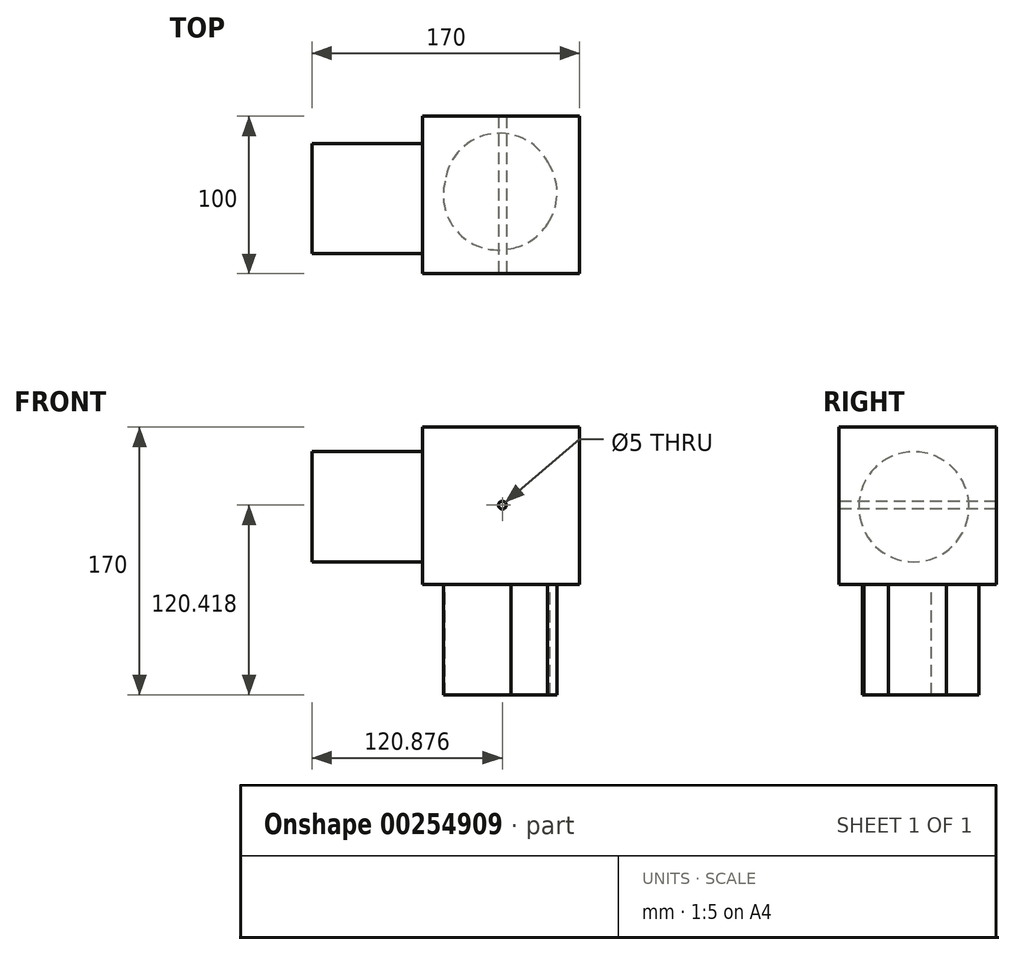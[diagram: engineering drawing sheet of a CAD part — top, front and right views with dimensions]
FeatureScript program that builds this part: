
annotation { "Feature Type Name" : "Feature", "Feature Type Description" : "" }
export const myFeature = defineFeature(function(context is Context, id is Id, definition is map)
    precondition{}
    {
        {
            var Q0;
            Q0=qCreatedBy(makeId("Front.planeOp"),FACE);
            var sketch = newSketch(context, id + "F0", { "sketchPlane" : qUnion([Q0])});
            skLineSegment(sketch, "E0.bottom", {"start": v(0, 0) * mm, "end": v(100, 0) * mm});
            skLineSegment(sketch, "E0.top", {"start": v(0, 100) * mm, "end": v(100, 100) * mm});
            skLineSegment(sketch, "E0.left", {"start": v(0, 0) * mm, "end": v(0, 100) * mm});
            skLineSegment(sketch, "E0.right", {"start": v(100, 0) * mm, "end": v(100, 100) * mm});
            skSolve(sketch);
        }
        {
            var Q0;
            Q0 = qSketchRegion(id + "F0", true);
            extrude(context, id + "F1", {"entities" : qUnion([Q0]), "depth" : 100 * mm});
        }
        {
            var Q0;
            Q0=qCreatedBy(makeId("Top.planeOp"),FACE);
            var sketch = newSketch(context, id + "F2", { "sketchPlane" : qUnion([Q0])});
            skCircle(sketch, "E1", {"center": v(48.35, -50) * mm, "radius": 35 * mm});
            skSolve(sketch);
        }
        {
            var Q0;
            Q0 = qSketchRegion(id + "F2", true);
            extrude(context, id + "F3", {"entities" : qUnion([Q0]), "operationType" : NewBodyOperationType.ADD, "oppositeDirection" : true, "depth" : 70 * mm});
        }
        {
            var Q0;
            Q0=qCreatedBy(makeId("Top.planeOp"),FACE);
            var sketch = newSketch(context, id + "F4", { "sketchPlane" : qUnion([Q0])});
            skCircle(sketch, "E2", {"center": v(49.17, -45.86) * mm, "radius": 35 * mm});
            skSolve(sketch);
        }
        {
            var Q0;
            Q0 = qSketchRegion(id + "F4", true);
            extrude(context, id + "F5", {"entities" : qUnion([Q0]), "operationType" : NewBodyOperationType.ADD, "oppositeDirection" : true, "depth" : 70 * mm});
        }
        {
            var Q0;
            Q0=qCreatedBy(makeId("Top.planeOp"),FACE);
            var sketch = newSketch(context, id + "F6", { "sketchPlane" : qUnion([Q0])});
            skCircle(sketch, "E3", {"center": v(48.55, -49.59) * mm, "radius": 35 * mm});
            skSolve(sketch);
        }
        {
            var Q0;
            Q0 = qSketchRegion(id + "F6", true);
            extrude(context, id + "F7", {"entities" : qUnion([Q0]), "operationType" : NewBodyOperationType.ADD, "oppositeDirection" : true, "depth" : 70 * mm});
        }
        {
            var Q0;
            Q0=qCreatedBy(makeId("Top.planeOp"),FACE);
            var sketch = newSketch(context, id + "F8", { "sketchPlane" : qUnion([Q0])});
            skCircle(sketch, "E4", {"center": v(50.63, -48.76) * mm, "radius": 35 * mm});
            skSolve(sketch);
        }
        {
            var Q0;
            Q0 = qSketchRegion(id + "F8", true);
            extrude(context, id + "F9", {"entities" : qUnion([Q0]), "operationType" : NewBodyOperationType.ADD, "oppositeDirection" : true, "depth" : 70 * mm});
        }
        {
            var Q0;
            Q0=qCreatedBy(makeId("Right.planeOp"),FACE);
            var sketch = newSketch(context, id + "F10", { "sketchPlane" : qUnion([Q0])});
            skCircle(sketch, "E5", {"center": v(-52.28, 49.4) * mm, "radius": 35 * mm});
            skSolve(sketch);
        }
        {
            var Q0;
            Q0=qCreatedBy(makeId("Top.planeOp"),FACE);
            var sketch = newSketch(context, id + "F11", { "sketchPlane" : qUnion([Q0])});
            skCircle(sketch, "E6", {"center": v(50.04, -49.65) * mm, "radius": 35 * mm});
            skSolve(sketch);
        }
        {
            var Q0;
            Q0 = qSketchRegion(id + "F11", true);
            extrude(context, id + "F12", {"entities" : qUnion([Q0]), "operationType" : NewBodyOperationType.ADD, "oppositeDirection" : true, "depth" : 70 * mm});
        }
        {
            var Q0;
            Q0=makeQuery(id+"F1.opExtrude","SWEPT_FACE",FACE,{"disambiguationData":[OSD([sQuery(id+"F0.wireOp",EDGE,"E0.top")])]});
            var sketch = newSketch(context, id + "F13", { "sketchPlane" : qUnion([Q0])});
            skCircle(sketch, "E7", {"center": v(49.72, -51.42) * mm, "radius": 35 * mm});
            skSolve(sketch);
        }
        {
            var Q0;
            Q0 = qSketchRegion(id + "F13", true);
            extrude(context, id + "F14", {"entities" : qUnion([Q0]), "operationType" : NewBodyOperationType.ADD, "oppositeDirection" : true, "depth" : 25 * mm});
        }
        {
            var Q0;
            Q0=makeQuery(id+"F10.imprint","IMPRINT",FACE,{"disambiguationData":[TD([[makeQuery(id+"F10.imprint","IMPRINT",EDGE,{"derivedFrom":sQuery(id+"F10.wireOp",EDGE,"E5")}),1.0]])]});
            extrude(context, id + "F15", {"entities" : qUnion([Q0]), "operationType" : NewBodyOperationType.ADD, "oppositeDirection" : true, "depth" : 70 * mm});
        }
        {
            var Q0;
            Q0=makeQuery(id+"F1.opExtrude","CAP_FACE",FACE,{"disambiguationData":[OSD([sQuery(id+"F0.wireOp",EDGE,"E0.bottom"),sQuery(id+"F0.wireOp",EDGE,"E0.top"),sQuery(id+"F0.wireOp",EDGE,"E0.left"),sQuery(id+"F0.wireOp",EDGE,"E0.right")])],"isStart":false});
            var sketch = newSketch(context, id + "F16", { "sketchPlane" : qUnion([Q0])});
            skPoint(sketch, "E8", {"position": v(50.88, 50.42) * mm});
            skSolve(sketch);
        }
        {
            var Q0;
            Q0=sQuery(id+"F16.wireOp",VERTEX,"E8");
            var Q1;
            Q1=makeQuery(id+"F1.opExtrude","SWEPT_BODY",BODY,{"disambiguationData":[OSD([sQuery(id+"F0.wireOp",EDGE,"E0.bottom"),sQuery(id+"F0.wireOp",EDGE,"E0.top"),sQuery(id+"F0.wireOp",EDGE,"E0.left"),sQuery(id+"F0.wireOp",EDGE,"E0.right")])]});
            hole(context, id + "F17", {"style" : HoleStyle.SIMPLE, "endStyle" : HoleEndStyle.THROUGH, "holeDiameter" : 5 * mm, "tappedDepth" : 12 * mm, "tapClearance" : 3, "locations" : qUnion([Q0]), "scope" : qUnion([Q1])});
        }
    });
